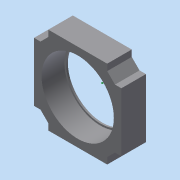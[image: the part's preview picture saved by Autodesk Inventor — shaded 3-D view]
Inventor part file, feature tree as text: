
AUTODESK INVENTOR PART (.ipt)
format: ipt  version: 2019.4 (Build 234330000, 330)  size: 169,984 bytes
history: native  units: mm
features: extrude x3, sketch x3, projected_geometry x2, hole x1
ambient origin geometry x8: Origin, YZ Plane, XZ Plane, XY Plane, X Axis, Y Axis, Z Axis, Center Point
bodies: Solid1 (feature_tree)
feature tree (9):
  extrude  "Thickness"  Depth=3.14mm
  hole  "Hole1"  [1 undecoded]
  extrude  "Extrusion2"  Depth=1.0mm
  extrude  "Extrusion3"  Depth=1.0mm TaperAngle=0.0deg
  sketch  "Sketch1"  dims[d0=45.0deg d1=3.14mm]
  sketch  "Sketch2"  dims[d2=3.66mm d3=16.8mm]
  projected_geometry  "Projected Loop1"
  sketch  "Sketch3"  dims[d5=0.0mm d20=10.0mm d21=10.0mm d8=41.2mm d9=6.0mm d10=7.0mm d11=3.0mm d12=90.0deg d13=8.0mm d14=0.0mm d17=1.0mm d18=1.0mm d19=0.0mm d22=50.0mm d23=10.0mm d24=0.0mm]
  projected_geometry  "Projected Loop2"
note: 1 required parameter value undecoded (feature->parameter linkage not recoverable at this tier; creation-order binding heuristic only, values carry confidence <= 0.55)
